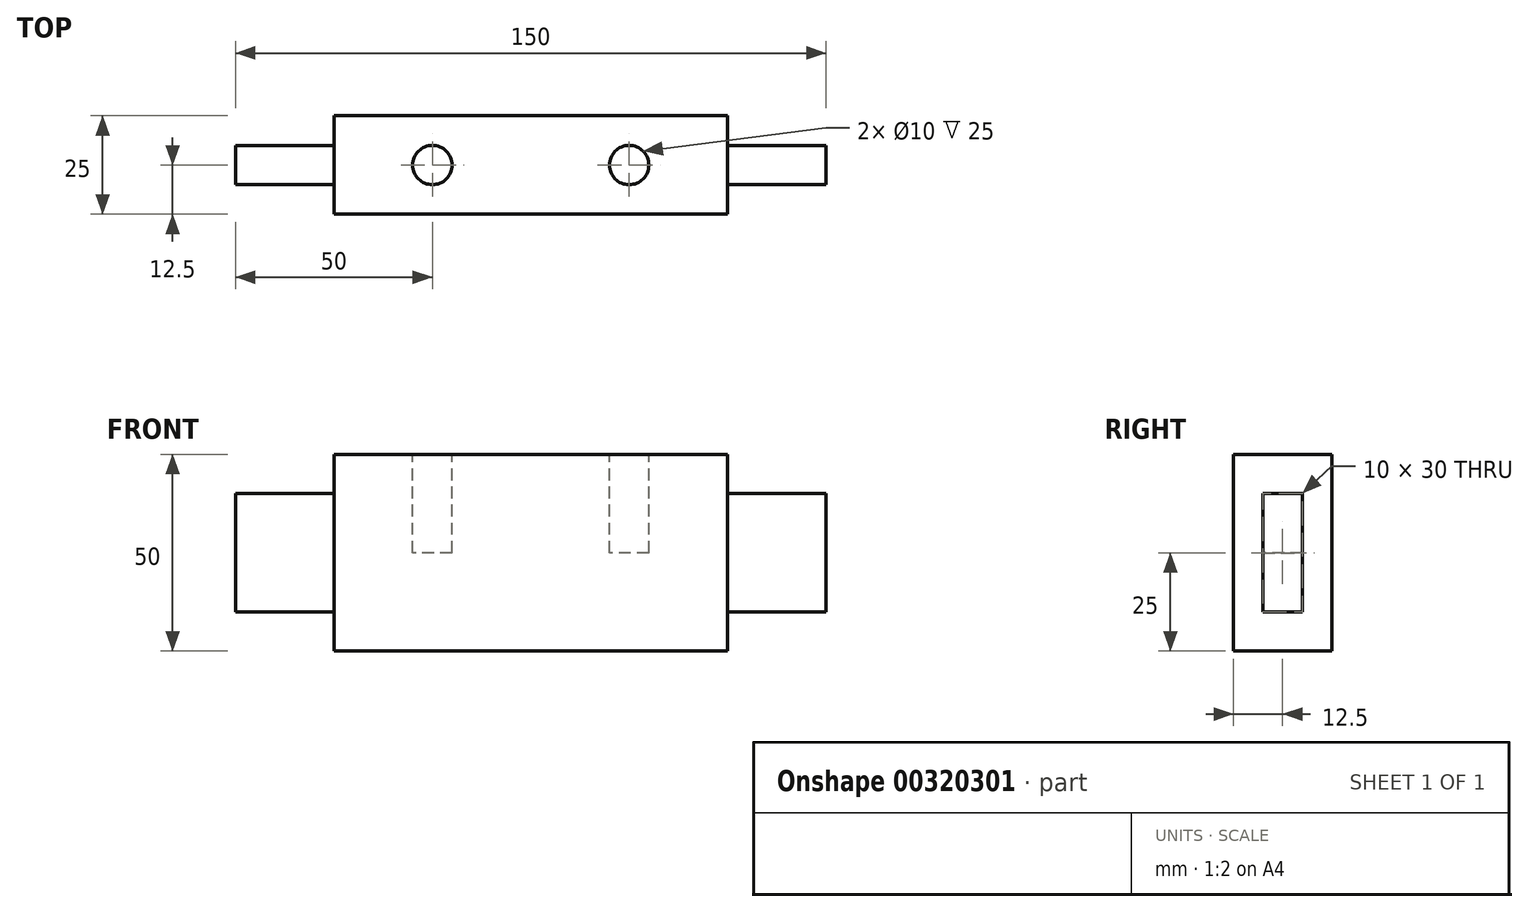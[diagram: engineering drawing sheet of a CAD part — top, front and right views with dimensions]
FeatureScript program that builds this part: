
annotation { "Feature Type Name" : "Feature", "Feature Type Description" : "" }
export const myFeature = defineFeature(function(context is Context, id is Id, definition is map)
    precondition{}
    {
        {
            var Q0;
            Q0=qCreatedBy(makeId("Front.planeOp"),FACE);
            var sketch = newSketch(context, id + "F0", { "sketchPlane" : qUnion([Q0])});
            skLineSegment(sketch, "E0.bottom", {"start": v(-50, 25) * mm, "end": v(50, 25) * mm});
            skLineSegment(sketch, "E0.top", {"start": v(-50, -25) * mm, "end": v(50, -25) * mm});
            skLineSegment(sketch, "E0.left", {"start": v(-50, 25) * mm, "end": v(-50, -25) * mm});
            skLineSegment(sketch, "E0.right", {"start": v(50, 25) * mm, "end": v(50, -25) * mm});
            skPoint(sketch, "E0.middle", {"position": v(0, 0) * mm});
            skSolve(sketch);
        }
        {
            var Q0;
            Q0=makeQuery(id+"F0.imprint","IMPRINT",FACE,{"disambiguationData":[TD([[makeQuery(id+"F0.imprint","IMPRINT",EDGE,{"derivedFrom":sQuery(id+"F0.wireOp",EDGE,"E0.bottom")}),-1.0]])]});
            extrude(context, id + "F1", {"entities" : qUnion([Q0]), "depth" : 25 * mm});
        }
        {
            var Q0;
            Q0=makeQuery(id+"F1.opExtrude","SWEPT_FACE",FACE,{"disambiguationData":[OSD([sQuery(id+"F0.wireOp",EDGE,"E0.left")])]});
            var sketch = newSketch(context, id + "F2", { "sketchPlane" : qUnion([Q0])});
            skLineSegment(sketch, "E1.bottom", {"start": v(17.5, 15) * mm, "end": v(7.5, 15) * mm});
            skLineSegment(sketch, "E1.top", {"start": v(17.5, -15) * mm, "end": v(7.5, -15) * mm});
            skLineSegment(sketch, "E1.left", {"start": v(17.5, 15) * mm, "end": v(17.5, -15) * mm});
            skLineSegment(sketch, "E1.right", {"start": v(7.5, 15) * mm, "end": v(7.5, -15) * mm});
            skPoint(sketch, "E1.middle", {"position": v(12.5, 0) * mm});
            skLineSegment(sketch, "E2", {"start": v(17.5, 0) * mm, "end": v(25, 0) * mm, "construction": true});
            skLineSegment(sketch, "E3", {"start": v(12.5, 15) * mm, "end": v(12.5, 25) * mm, "construction": true});
            skLineSegment(sketch, "E4", {"start": v(0, 0) * mm, "end": v(7.5, 0) * mm, "construction": true});
            skLineSegment(sketch, "E5", {"start": v(12.5, -15) * mm, "end": v(12.5, -25) * mm, "construction": true});
            skPoint(sketch, "E5.endSnap0", {"position": v(12.5, -15) * mm});
            skSolve(sketch);
        }
        {
            var Q0;
            Q0=makeQuery(id+"F2.imprint","IMPRINT",FACE,{"disambiguationData":[TD([[makeQuery(id+"F2.imprint","IMPRINT",EDGE,{"derivedFrom":sQuery(id+"F2.wireOp",EDGE,"E1.bottom")}),1.0]])]});
            extrude(context, id + "F3", {"entities" : qUnion([Q0]), "operationType" : NewBodyOperationType.ADD, "depth" : 25 * mm});
        }
        {
            var Q0;
            Q0=makeQuery(id+"F1.opExtrude","SWEPT_BODY",BODY,{"disambiguationData":[OSD([sQuery(id+"F0.wireOp",EDGE,"E0.bottom"),sQuery(id+"F0.wireOp",EDGE,"E0.top"),sQuery(id+"F0.wireOp",EDGE,"E0.left"),sQuery(id+"F0.wireOp",EDGE,"E0.right")])]});
            var Q1;
            Q1=qCreatedBy(makeId("Right.planeOp"),FACE);
            mirror(context, id + "F4", {"operationType" : NewBodyOperationType.ADD, "entities" : qUnion([Q0]), "mirrorPlane" : qUnion([Q1])});
        }
        {
            var Q0;
            Q0=makeQuery(id+"F1.opExtrude","SWEPT_FACE",FACE,{"disambiguationData":[OSD([sQuery(id+"F0.wireOp",EDGE,"E0.bottom")])]});
            var sketch = newSketch(context, id + "F5", { "sketchPlane" : qUnion([Q0])});
            skLineSegment(sketch, "E6", {"start": v(0, 0) * mm, "end": v(0, -25) * mm, "construction": true});
            skLineSegment(sketch, "E7", {"start": v(0, -12.5) * mm, "end": v(50, -12.5) * mm, "construction": true});
            skLineSegment(sketch, "E8", {"start": v(0, -12.5) * mm, "end": v(-50, -12.5) * mm, "construction": true});
            skCircle(sketch, "E9", {"center": v(-25, -12.5) * mm, "radius": 5 * mm});
            skCircle(sketch, "E10", {"center": v(25, -12.5) * mm, "radius": 5 * mm});
            skSolve(sketch);
        }
        {
            var Q0;
            Q0=makeQuery(id+"F5.imprint","IMPRINT",FACE,{"disambiguationData":[TD([[makeQuery(id+"F5.imprint","IMPRINT",EDGE,{"derivedFrom":sQuery(id+"F5.wireOp",EDGE,"E9")}),1.0]])]});
            var Q1;
            Q1=makeQuery(id+"F5.imprint","IMPRINT",FACE,{"disambiguationData":[TD([[makeQuery(id+"F5.imprint","IMPRINT",EDGE,{"derivedFrom":sQuery(id+"F5.wireOp",EDGE,"E10")}),1.0]])]});
            extrude(context, id + "F6", {"entities" : qUnion([Q0, Q1]), "operationType" : NewBodyOperationType.REMOVE, "oppositeDirection" : true, "depth" : 25 * mm});
        }
    });
